# Revit family: QF_ELECTROLUXPROFESSIONAL_1LSNJ5_IC64825_S
name_source: partatom
category: Attrezzature speciali
units: mm (PartAtom-declared; Revit-internal decimal feet)

## family parameters
Basato su piano di lavoro = No
Condiviso = No
Punto di calcolo locali = No
Quota connettore circolare = Usa diametro
Sempre verticale = Sì
Taglio con vuoti quando caricato = No
Tipo di parte = Normale

## types (1)
- 9882030281
    Cycle = 60 Hz
    Depth Actual = 1110 mm  [stored 3.64173 ft]
    Descrizione = IRONER CYLINDER IC64825 2540MM ACTIVE STEAM CE 208-240/60/3 4MM SST CYL. EN, ES, PO
    Gas KW = 0
    Height Actual = 1270 mm  [stored 4.16667 ft]
    Item Number = 1L0H8X
    Latent Heat Output = 0.0
    Length Actual = 3205 mm  [stored 10.5151 ft]
    Modello = IC64825
    Phase = 3
    Produttore = Electrolux Professional
    Prospetto di default = 0 mm  [stored 0 ft]
    Sensible Heat Output = 0.0
    Steam Pounds per Hour = 110
    URL = www.electroluxprofessional.com
    Volts = 240 V
    Watts = 2000 W
    Weight = 860

note: [stored X ft] marks values corroborated as IEEE doubles in the binary element streams (Revit-internal decimal feet)

## geometry (parser evidence)
native form markers: Sweep x11
no freeform markers — native parametric forms only
